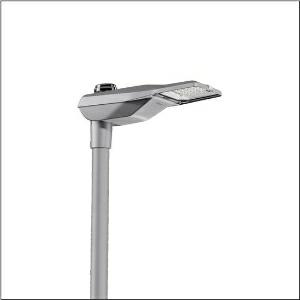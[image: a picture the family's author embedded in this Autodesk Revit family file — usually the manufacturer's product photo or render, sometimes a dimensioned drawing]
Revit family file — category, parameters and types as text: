
# Revit family: streetlight_sl_21_micro___stw1_0a_5xe5e47n08db_5020
name_source: partatom
category: Lighting Fixtures
units: mm (PartAtom-declared; Revit-internal decimal feet)

## family parameters
Cut with Voids When Loaded = No
Host = Face
Light Source = No
Part Type = Normal
Room Calculation Point = No
Round Connector Dimension = Use Diameter
Shared = No

## types (1)
- --- (1 x LED, 5320 lm, 39.1 W, 4000K)
    Apparent Load = 39 VA
    CIE Flux Codes = 38 75 98 100 100
    Color Rendering = 70
    Color Temperature = 4000K
    Default Elevation = 1800 mm
    Description = Streetlight SL 21 micro, mast luminaire, primary light control with lens, of PMMA, primary optical cover: cover, of toughened safety glass, transparent, light distribution: STW1.0a, light emission: direct distribution, primary light characteristic: asymmetric, installation type: post-top, LED, 3G 1.5mm², High Power LED, rated luminous flux: 5.320lm, luminous efficacy: 136lm/W, light colour: 740, colour temperature: 4000K, control gear: NEMA (7pin), control: overheat protection, pre-setting: linear dimming characteristic, constant luminous flux control, time-dependent luminous flux control, flexible luminous flux parameterisation, mains connection: 230..240V, AC, 50/60Hz, connection cable pre-assembled, cable length: 6,5m, wiring characteristics: H07RN-F, start of lifetime: 39W, end of service life: 41W, reduction: 18W, luminaire housing, of diecast aluminium (EN AC-44300), powder-coated, Siteco® metallic grey (DB 702S), corrosivity category C5 mid according to DIN EN ISO 12944, multi-level sealing system, sealing non-destructively replaceable, inclination adjustable: 0°, 5°, 10°, 15°, length: 528mm, width: 235mm, height: 110mm, spigot size: 76/60mm (post-top), mounting height: 4..8m, protection rating (complete): IP66, insulation class (complete): insulation class I (protective earthing), certification: CE, ENEC, ENEC+, VDE, impact resistance: IK10, permissible operating ambient temperature for outdoor applications: -40..+50°C, standard-compliant lighting for roads and squares, packaging unit: 1 piece

Light Distribution: STW1.0a
    Height = 110 mm
    Lamp = 1 x LED
    Lamp Light Flux = 5320 lm
    Lamp Power = 39.1 W
    Lamp count = 1
    Length = 528 mm
    Luminous efficacy = 136 lm/W
    Manufacturer = Siteco
    ModVariant = No
    Model = 5XE5E47N08DB
    Number of Poles = 1
    OnlyDefault = Yes
    Power Factor = 1
    Product Name = Streetlight SL 21 micro | STW1.0a
    Product group = mast luminaire | pylon top
    ProductGroupID = 6100
    Protection Class = Protection class I
    Protection Degree = IP 66
    RLX_Detail_Level = 1
    RLX_Emergency_Light_Flux = 0 lm
    RLX_Emergency_Type = 0
    RLX_Emergency_Type_DB = No
    RlxData = <blob elided: 99213 chars, md5=d572b55c>
    Socket = socket
    Standby Power = 0 W
    System Light Flux = 5320 lm
    System Power = 39 W
    Type Comments = factory setting: luminous flux: 100 % | dim-lin: 254 | 765 mA
    Type Image = l_1294375.jpg
    URL = http://relux.com
    VarID = @adj_157233
    Voltage = 0 V
    Weight = 0.00 kg
    Width = 235 mm

## geometry (parser evidence)
native form markers: Blend x4, Sweep x8
no freeform markers — native parametric forms only
